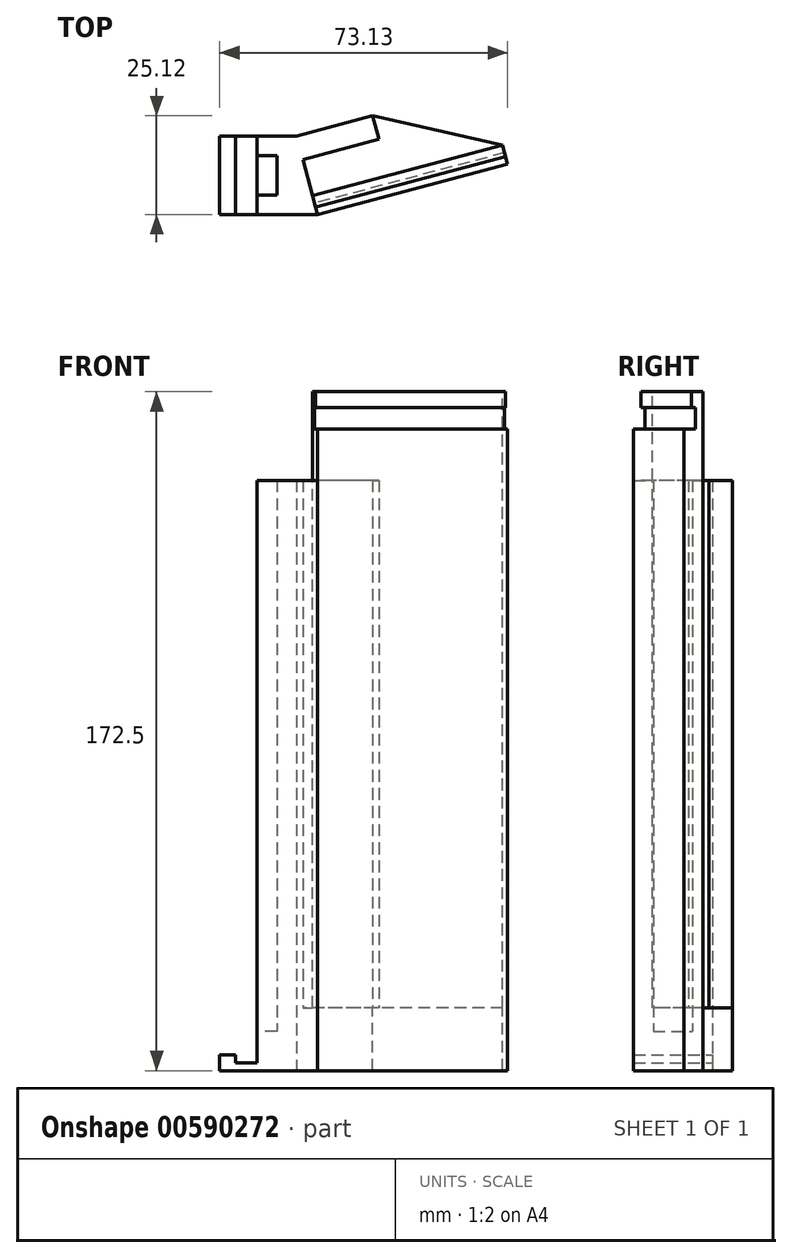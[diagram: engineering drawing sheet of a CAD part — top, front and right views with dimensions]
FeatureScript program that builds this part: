
annotation { "Feature Type Name" : "Feature", "Feature Type Description" : "" }
export const myFeature = defineFeature(function(context is Context, id is Id, definition is map)
    precondition{}
    {
        {
            var Q0;
            Q0=qCreatedBy(makeId("Top.planeOp"),FACE);
            var sketch = newSketch(context, id + "F0", { "sketchPlane" : qUnion([Q0])});
            skLineSegment(sketch, "E0.bottom", {"start": v(0, 0) * mm, "end": v(4, 0) * mm});
            skLineSegment(sketch, "E0.top", {"start": v(0, 20) * mm, "end": v(4, 20) * mm});
            skLineSegment(sketch, "E0.left", {"start": v(0, 0) * mm, "end": v(0, 20) * mm});
            skLineSegment(sketch, "E0.right", {"start": v(4, 0) * mm, "end": v(4, 20) * mm});
            skSolve(sketch);
        }
        {
            var Q0;
            Q0 = qSketchRegion(id + "F0", true);
            extrude(context, id + "F1", {"entities" : qUnion([Q0]), "depth" : 4 * mm, "offsetDistance" : 25 * mm});
        }
        {
            var Q0;
            Q0=qCreatedBy(makeId("Top.planeOp"),FACE);
            var sketch = newSketch(context, id + "F2", { "sketchPlane" : qUnion([Q0])});
            skLineSegment(sketch, "E1.bottom", {"start": v(4, 0) * mm, "end": v(9.5, 0) * mm});
            skLineSegment(sketch, "E1.top", {"start": v(4, 20) * mm, "end": v(9.5, 20) * mm});
            skLineSegment(sketch, "E1.left", {"start": v(4, 0) * mm, "end": v(4, 20) * mm});
            skLineSegment(sketch, "E1.right", {"start": v(9.5, 0) * mm, "end": v(9.5, 20) * mm});
            skSolve(sketch);
        }
        {
            var Q0;
            Q0 = qSketchRegion(id + "F2", true);
            extrude(context, id + "F3", {"entities" : qUnion([Q0]), "operationType" : NewBodyOperationType.ADD, "depth" : 2 * mm, "offsetDistance" : 25 * mm});
        }
        {
            var Q0;
            Q0=qCreatedBy(makeId("Top.planeOp"),FACE);
            var sketch = newSketch(context, id + "F4", { "sketchPlane" : qUnion([Q0])});
            skLineSegment(sketch, "E2.bottom", {"start": v(9.5, 0) * mm, "end": v(14.5, 0) * mm});
            skLineSegment(sketch, "E2.top", {"start": v(9.5, 20) * mm, "end": v(14.5, 20) * mm});
            skLineSegment(sketch, "E2.left", {"start": v(9.5, 0) * mm, "end": v(9.5, 20) * mm});
            skLineSegment(sketch, "E2.right", {"start": v(14.5, 0) * mm, "end": v(14.5, 20) * mm});
            skSolve(sketch);
        }
        {
            var Q0;
            Q0 = qSketchRegion(id + "F4", true);
            extrude(context, id + "F5", {"entities" : qUnion([Q0]), "operationType" : NewBodyOperationType.ADD, "depth" : 10 * mm, "offsetDistance" : 25 * mm});
        }
        {
            var Q0;
            Q0=qCreatedBy(makeId("Top.planeOp"),FACE);
            var sketch = newSketch(context, id + "F6", { "sketchPlane" : qUnion([Q0])});
            skLineSegment(sketch, "E3.bottom", {"start": v(14.5, 20) * mm, "end": v(19.5, 20) * mm});
            skLineSegment(sketch, "E3.top", {"start": v(14.5, 0) * mm, "end": v(19.5, 0) * mm});
            skLineSegment(sketch, "E3.left", {"start": v(14.5, 20) * mm, "end": v(14.5, 0) * mm});
            skLineSegment(sketch, "E3.right", {"start": v(19.5, 20) * mm, "end": v(19.5, 0) * mm});
            skLineSegment(sketch, "E4", {"start": v(19.5, 20) * mm, "end": v(24.8, 0) * mm});
            skLineSegment(sketch, "E5", {"start": v(24.8, 0) * mm, "end": v(19.5, 0) * mm});
            skSolve(sketch);
        }
        {
            var Q0;
            Q0 = qSketchRegion(id + "F6", true);
            extrude(context, id + "F7", {"entities" : qUnion([Q0]), "operationType" : NewBodyOperationType.ADD, "depth" : 150 * mm, "offsetDistance" : 25 * mm});
        }
        {
            var Q0;
            Q0=makeQuery(id+"F5.opExtrude","CAP_FACE",FACE,{"disambiguationData":[OSD([sQuery(id+"F4.wireOp",EDGE,"E2.bottom"),sQuery(id+"F4.wireOp",EDGE,"E2.top"),sQuery(id+"F4.wireOp",EDGE,"E2.left"),sQuery(id+"F4.wireOp",EDGE,"E2.right")])],"isStart":false});
            var sketch = newSketch(context, id + "F8", { "sketchPlane" : qUnion([Q0])});
            skLineSegment(sketch, "E6.bottom", {"start": v(9.5, 20) * mm, "end": v(14.5, 20) * mm});
            skLineSegment(sketch, "E6.top", {"start": v(9.5, 15) * mm, "end": v(14.5, 15) * mm});
            skLineSegment(sketch, "E6.left", {"start": v(9.5, 20) * mm, "end": v(9.5, 15) * mm});
            skLineSegment(sketch, "E6.right", {"start": v(14.5, 20) * mm, "end": v(14.5, 15) * mm});
            skLineSegment(sketch, "E7.bottom", {"start": v(14.5, 0) * mm, "end": v(9.5, 0) * mm});
            skLineSegment(sketch, "E7.top", {"start": v(14.5, 5) * mm, "end": v(9.5, 5) * mm});
            skLineSegment(sketch, "E7.left", {"start": v(14.5, 0) * mm, "end": v(14.5, 5) * mm});
            skLineSegment(sketch, "E7.right", {"start": v(9.5, 0) * mm, "end": v(9.5, 5) * mm});
            skSolve(sketch);
        }
        {
            var Q0;
            Q0 = qSketchRegion(id + "F8", true);
            extrude(context, id + "F9", {"entities" : qUnion([Q0]), "operationType" : NewBodyOperationType.ADD, "depth" : 140 * mm, "offsetDistance" : 25 * mm});
        }
        {
            var Q0;
            Q0=makeQuery(id+"F7.opExtrude","SWEPT_FACE",FACE,{"disambiguationData":[OSD([sQuery(id+"F6.wireOp",EDGE,"E4")])]});
            var sketch = newSketch(context, id + "F10", { "sketchPlane" : qUnion([Q0])});
            skLineSegment(sketch, "E8.bottom", {"start": v(-6.35, 0) * mm, "end": v(-1.35, 0) * mm});
            skLineSegment(sketch, "E8.top", {"start": v(-6.35, 163) * mm, "end": v(-1.35, 163) * mm});
            skLineSegment(sketch, "E8.left", {"start": v(-6.35, 0) * mm, "end": v(-6.35, 163) * mm});
            skLineSegment(sketch, "E8.right", {"start": v(-1.35, 0) * mm, "end": v(-1.35, 163) * mm});
            skSolve(sketch);
        }
        {
            var Q0;
            Q0 = qSketchRegion(id + "F10", true);
            extrude(context, id + "F11", {"entities" : qUnion([Q0]), "operationType" : NewBodyOperationType.ADD, "depth" : 50 * mm, "offsetDistance" : 25 * mm});
        }
        {
            var Q0;
            Q0=makeQuery(id+"F7.opExtrude","SWEPT_FACE",FACE,{"disambiguationData":[OSD([sQuery(id+"F6.wireOp",EDGE,"E4")])]});
            var sketch = newSketch(context, id + "F12", { "sketchPlane" : qUnion([Q0])});
            skLineSegment(sketch, "E9.bottom", {"start": v(14.34, 150) * mm, "end": v(8.14, 150) * mm});
            skLineSegment(sketch, "E9.top", {"start": v(14.34, 0) * mm, "end": v(8.14, 0) * mm});
            skLineSegment(sketch, "E9.left", {"start": v(14.34, 150) * mm, "end": v(14.34, 0) * mm});
            skLineSegment(sketch, "E9.right", {"start": v(8.14, 150) * mm, "end": v(8.14, 0) * mm});
            skLineSegment(sketch, "E10.bottom", {"start": v(8.14, 0) * mm, "end": v(-1.35, 0) * mm});
            skLineSegment(sketch, "E10.top", {"start": v(8.14, 16) * mm, "end": v(-1.35, 16) * mm});
            skLineSegment(sketch, "E10.left", {"start": v(8.14, 0) * mm, "end": v(8.14, 16) * mm});
            skLineSegment(sketch, "E10.right", {"start": v(-1.35, 0) * mm, "end": v(-1.35, 16) * mm});
            skSolve(sketch);
        }
        {
            var Q0;
            Q0 = qSketchRegion(id + "F12", true);
            extrude(context, id + "F13", {"entities" : qUnion([Q0]), "operationType" : NewBodyOperationType.ADD, "depth" : 20 * mm, "offsetDistance" : 25 * mm});
        }
        {
            var Q0;
            Q0=makeQuery(id+"F13.opExtrude","CAP_FACE",FACE,{"disambiguationData":[OSD([sQuery(id+"F12.wireOp",EDGE,"E9.bottom"),sQuery(id+"F12.wireOp",EDGE,"E9.top"),sQuery(id+"F12.wireOp",EDGE,"E9.left"),sQuery(id+"F12.wireOp",EDGE,"E9.right"),sQuery(id+"F12.wireOp",EDGE,"E10.bottom"),sQuery(id+"F12.wireOp",EDGE,"E10.top"),sQuery(id+"F12.wireOp",EDGE,"E10.right")])],"isStart":false});
            var sketch = newSketch(context, id + "F14", { "sketchPlane" : qUnion([Q0])});
            skLineSegment(sketch, "E11.bottom", {"start": v(-1.35, 16) * mm, "end": v(14.34, 16) * mm});
            skLineSegment(sketch, "E11.top", {"start": v(-1.35, 0) * mm, "end": v(14.34, 0) * mm});
            skLineSegment(sketch, "E11.left", {"start": v(-1.35, 16) * mm, "end": v(-1.35, 0) * mm});
            skLineSegment(sketch, "E11.right", {"start": v(14.34, 16) * mm, "end": v(14.34, 0) * mm});
            skSolve(sketch);
        }
        {
            var Q0;
            Q0 = qSketchRegion(id + "F14", true);
            extrude(context, id + "F15", {"entities" : qUnion([Q0]), "operationType" : NewBodyOperationType.ADD, "depth" : 30 * mm, "offsetDistance" : 25 * mm});
        }
        {
            var Q0;
            Q0=makeQuery(id+"F15.boolean.opBoolean","MERGE",FACE,{"derivedFrom":[makeQuery(id+"F13.opExtrude","SWEPT_FACE",FACE,{"disambiguationData":[OSD([sQuery(id+"F12.wireOp",EDGE,"E10.top")])]}),makeQuery(id+"F15.opExtrude","SWEPT_FACE",FACE,{"disambiguationData":[OSD([sQuery(id+"F14.wireOp",EDGE,"E11.bottom")])]})]});
            var sketch = newSketch(context, id + "F16", { "sketchPlane" : qUnion([Q0])});
            skLineSegment(sketch, "E12", {"start": v(38.83, 25.12) * mm, "end": v(67.83, 32.8) * mm});
            skLineSegment(sketch, "E13", {"start": v(67.83, 32.8) * mm, "end": v(71.85, 17.64) * mm});
            skLineSegment(sketch, "E14", {"start": v(71.85, 17.64) * mm, "end": v(38.83, 25.12) * mm});
            skSolve(sketch);
        }
        {
            var Q0;
            Q0 = qSketchRegion(id + "F16", true);
            extrude(context, id + "F17", {"entities" : qUnion([Q0]), "operationType" : NewBodyOperationType.REMOVE, "oppositeDirection" : true, "depth" : 16 * mm, "offsetDistance" : 25 * mm});
        }
        {
            var Q0;
            Q0=makeQuery(id+"F11.opExtrude","SWEPT_FACE",FACE,{"disambiguationData":[OSD([sQuery(id+"F10.wireOp",EDGE,"E8.top")])]});
            var sketch = newSketch(context, id + "F18", { "sketchPlane" : qUnion([Q0])});
            skLineSegment(sketch, "E15", {"start": v(23.52, 4.83) * mm, "end": v(71.85, 17.64) * mm});
            skLineSegment(sketch, "E16", {"start": v(71.85, 17.64) * mm, "end": v(72.36, 15.7) * mm});
            skLineSegment(sketch, "E17", {"start": v(72.36, 15.7) * mm, "end": v(24.03, 2.9) * mm});
            skLineSegment(sketch, "E18", {"start": v(24.03, 2.9) * mm, "end": v(23.52, 4.83) * mm});
            skSolve(sketch);
        }
        {
            var Q0;
            Q0 = qSketchRegion(id + "F18", true);
            extrude(context, id + "F19", {"entities" : qUnion([Q0]), "operationType" : NewBodyOperationType.ADD, "depth" : 5.5 * mm, "offsetDistance" : 25 * mm});
        }
        {
            var Q0;
            Q0=makeQuery(id+"F19.opExtrude","CAP_FACE",FACE,{"disambiguationData":[OSD([sQuery(id+"F18.wireOp",EDGE,"E15"),sQuery(id+"F18.wireOp",EDGE,"E16"),sQuery(id+"F18.wireOp",EDGE,"E17"),sQuery(id+"F18.wireOp",EDGE,"E18")])],"isStart":false});
            var sketch = newSketch(context, id + "F20", { "sketchPlane" : qUnion([Q0])});
            skLineSegment(sketch, "E19", {"start": v(23.52, 4.83) * mm, "end": v(24.29, 1.93) * mm});
            skLineSegment(sketch, "E20", {"start": v(24.29, 1.93) * mm, "end": v(72.62, 14.74) * mm});
            skLineSegment(sketch, "E21", {"start": v(72.62, 14.74) * mm, "end": v(71.85, 17.64) * mm});
            skLineSegment(sketch, "E22", {"start": v(71.85, 17.64) * mm, "end": v(23.52, 4.83) * mm});
            skSolve(sketch);
        }
        {
            var Q0;
            Q0 = qSketchRegion(id + "F20", true);
            extrude(context, id + "F21", {"entities" : qUnion([Q0]), "operationType" : NewBodyOperationType.ADD, "depth" : 4 * mm, "offsetDistance" : 25 * mm});
        }
    });
